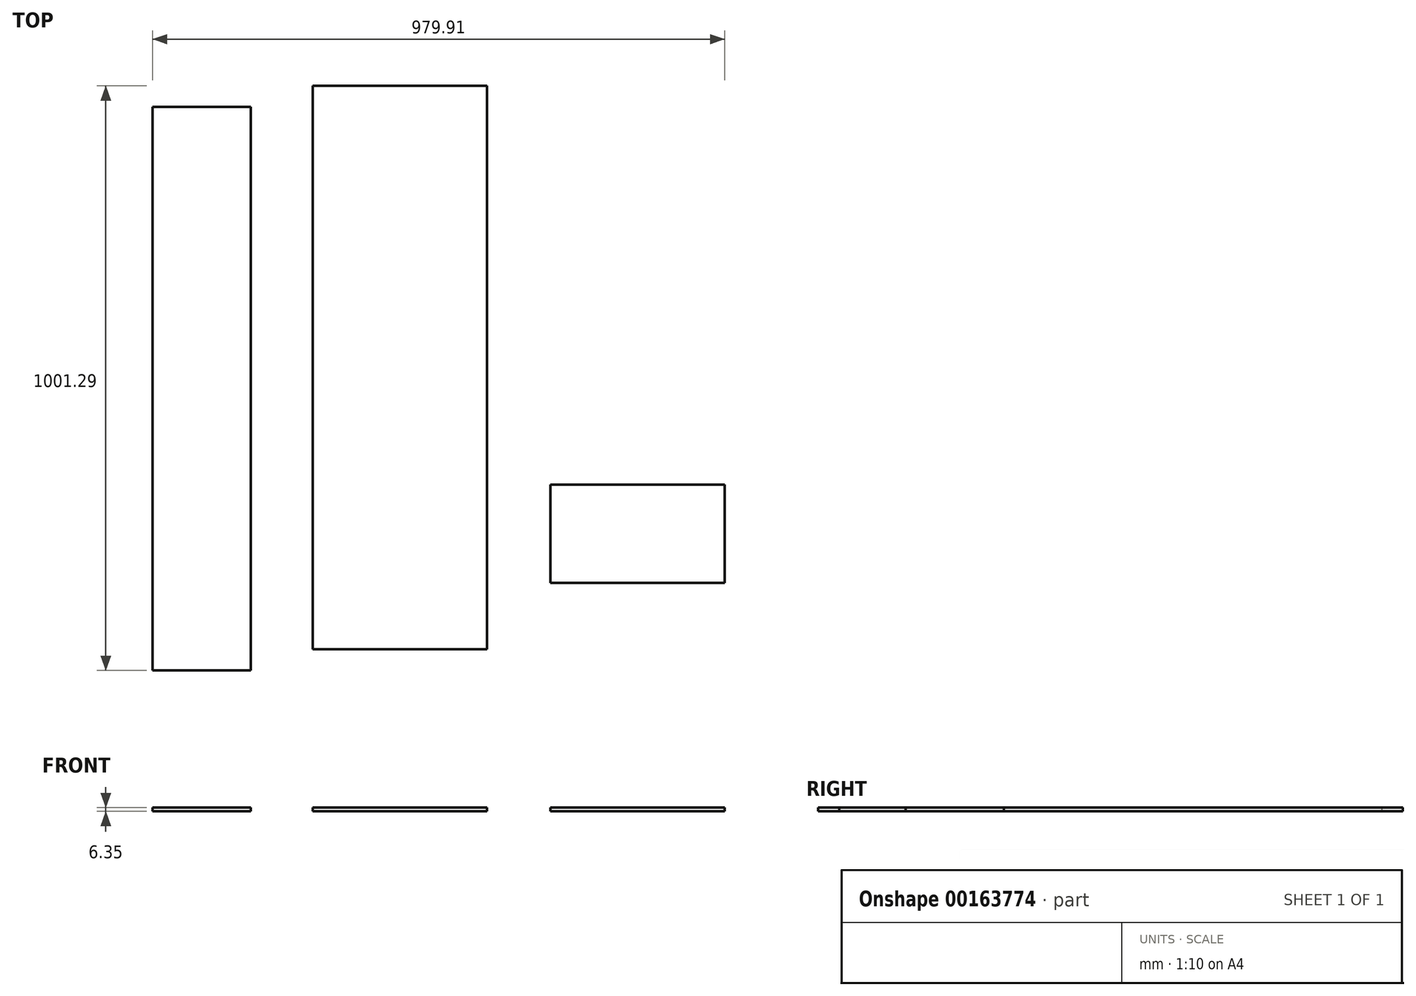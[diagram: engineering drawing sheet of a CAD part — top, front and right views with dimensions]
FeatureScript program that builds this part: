
annotation { "Feature Type Name" : "Feature", "Feature Type Description" : "" }
export const myFeature = defineFeature(function(context is Context, id is Id, definition is map)
    precondition{}
    {
        {
            var Q0;
            Q0=qCreatedBy(makeId("Top.planeOp"),FACE);
            var sketch = newSketch(context, id + "F0", { "sketchPlane" : qUnion([Q0])});
            skLineSegment(sketch, "E0.bottom", {"start": v(-183.34, -167.11) * mm, "end": v(-351.62, -167.11) * mm});
            skLineSegment(sketch, "E0.top", {"start": v(-183.34, 798.09) * mm, "end": v(-351.62, 798.09) * mm});
            skLineSegment(sketch, "E0.left", {"start": v(-183.34, -167.11) * mm, "end": v(-183.34, 798.09) * mm});
            skLineSegment(sketch, "E0.right", {"start": v(-351.62, -167.11) * mm, "end": v(-351.62, 798.09) * mm});
            skPoint(sketch, "E0.middle", {"position": v(-267.48, 315.49) * mm});
            skLineSegment(sketch, "E1.bottom", {"start": v(221.63, -131.02) * mm, "end": v(-76.82, -131.02) * mm});
            skLineSegment(sketch, "E1.top", {"start": v(221.63, 834.18) * mm, "end": v(-76.82, 834.18) * mm});
            skLineSegment(sketch, "E1.left", {"start": v(221.63, -131.02) * mm, "end": v(221.63, 834.18) * mm});
            skLineSegment(sketch, "E1.right", {"start": v(-76.82, -131.02) * mm, "end": v(-76.82, 834.18) * mm});
            skPoint(sketch, "E1.middle", {"position": v(72.4, 351.58) * mm});
            skLineSegment(sketch, "E2.bottom", {"start": v(628.3, -17.35) * mm, "end": v(329.84, -17.35) * mm});
            skLineSegment(sketch, "E2.top", {"start": v(628.3, 150.93) * mm, "end": v(329.84, 150.93) * mm});
            skLineSegment(sketch, "E2.left", {"start": v(628.3, -17.35) * mm, "end": v(628.3, 150.93) * mm});
            skLineSegment(sketch, "E2.right", {"start": v(329.84, -17.35) * mm, "end": v(329.84, 150.93) * mm});
            skPoint(sketch, "E2.middle", {"position": v(479.07, 66.79) * mm});
            skSolve(sketch);
        }
        {
            var Q0;
            Q0 = qSketchRegion(id + "F0", true);
            extrude(context, id + "F1", {"entities" : qUnion([Q0]), "depth" : 6.35 * mm, "offsetDistance" : 25.4 * mm});
        }
    });
